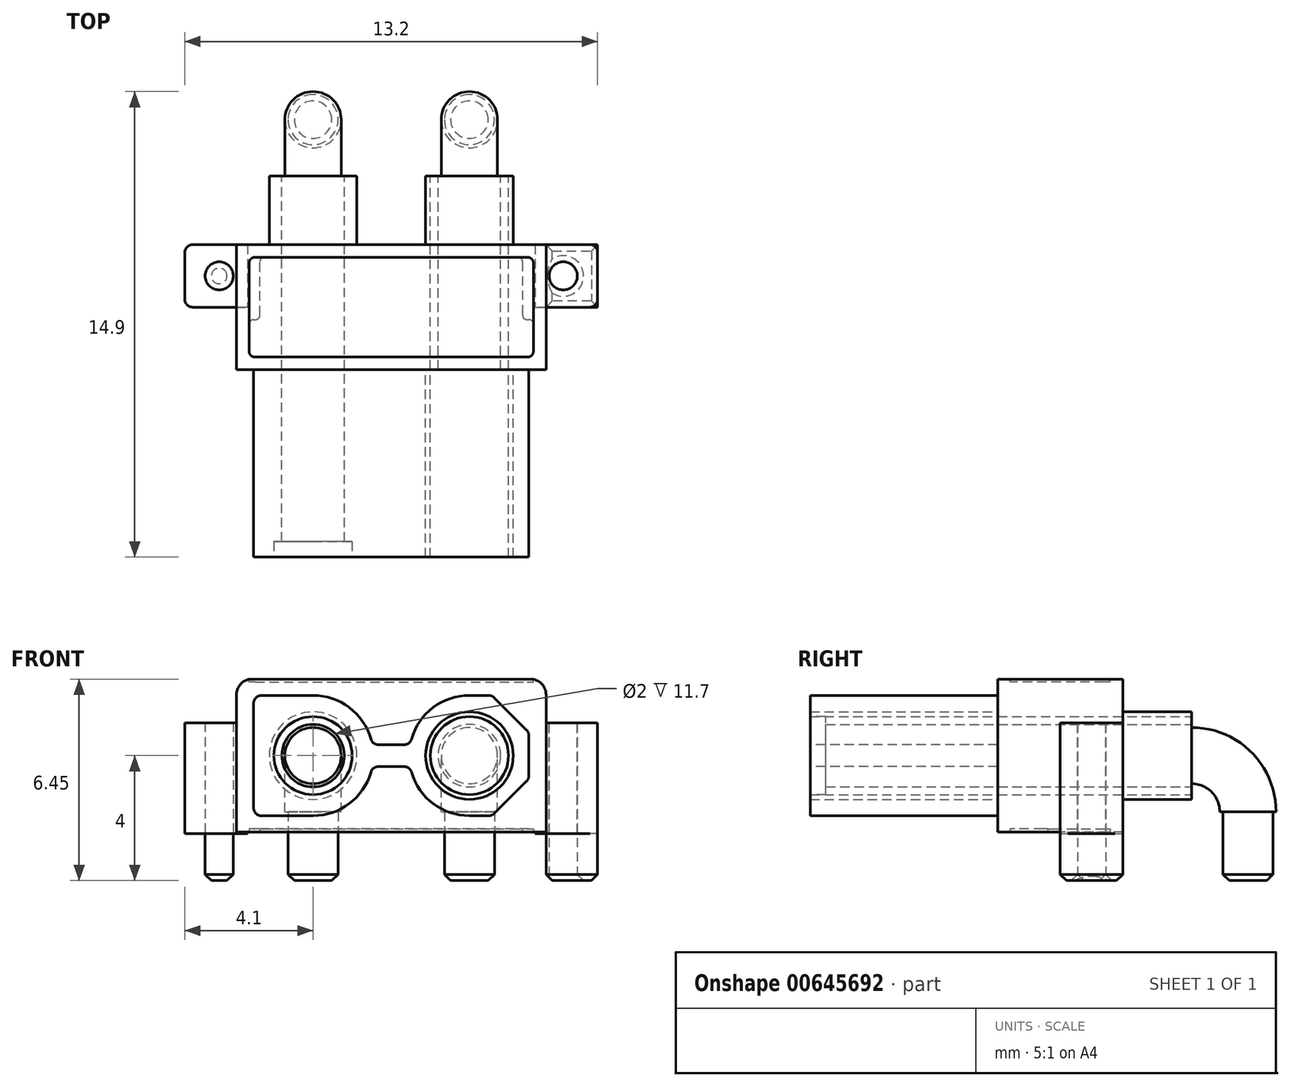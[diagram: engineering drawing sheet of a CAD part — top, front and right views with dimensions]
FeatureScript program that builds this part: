
annotation { "Feature Type Name" : "Feature", "Feature Type Description" : "" }
export const myFeature = defineFeature(function(context is Context, id is Id, definition is map)
    precondition{}
    {
        {
            var Q0;
            Q0=qCreatedBy(makeId("Front.planeOp"),FACE);
            var sketch = newSketch(context, id + "F0", { "sketchPlane" : qUnion([Q0])});
            skLineSegment(sketch, "E0", {"start": v(-2.5, 0) * mm, "end": v(2.5, 0) * mm, "construction": true});
            skCircle(sketch, "E1", {"center": v(2.5, 0) * mm, "radius": 1.25 * mm});
            skCircle(sketch, "E2", {"center": v(-2.5, 0) * mm, "radius": 1.25 * mm});
            skCircle(sketch, "E3", {"center": v(-2.5, 0) * mm, "radius": 1 * mm});
            skCircle(sketch, "E4", {"center": v(2.5, 0) * mm, "radius": 1 * mm});
            skSolve(sketch);
        }
        {
            var Q0;
            Q0=qCreatedBy(makeId("Front.planeOp"),FACE);
            var sketch = newSketch(context, id + "F1", { "sketchPlane" : qUnion([Q0])});
            skCircle(sketch, "E5.MirrorC", {"center": v(2.5, 0) * mm, "radius": 1.25 * mm});
            skCircle(sketch, "E6.MirrorC", {"center": v(-2.5, 0) * mm, "radius": 1.4 * mm});
            skLineSegment(sketch, "E7.MirrorCS", {"start": v(3.23, -1.93) * mm, "end": v(2.5, -1.93) * mm});
            skArc(sketch, "E8.MirrorCS", {"start": v(2.5, -1.93) * mm, "mid": v(1.27, -1.48) * mm, "end": v(0.6, -0.35) * mm});
            skCircle(sketch, "E9.MirrorC", {"center": v(-2.5, 0) * mm, "radius": 1.25 * mm});
            skArc(sketch, "E10.MirrorCS", {"start": v(-0.6, -0.35) * mm, "mid": v(-1.27, -1.48) * mm, "end": v(-2.5, -1.93) * mm});
            skCircle(sketch, "E11.MirrorC", {"center": v(2.5, 0) * mm, "radius": 1.4 * mm});
            skLineSegment(sketch, "E12.MirrorCS", {"start": v(0.6, 0.35) * mm, "end": v(-0.6, 0.35) * mm});
            skLineSegment(sketch, "E13.MirrorCS", {"start": v(-0.6, -0.35) * mm, "end": v(0.6, -0.35) * mm});
            skLineSegment(sketch, "E14.MirrorCS", {"start": v(2.5, 1.93) * mm, "end": v(3.23, 1.93) * mm});
            skLineSegment(sketch, "E15.MirrorCS", {"start": v(3.23, 1.92) * mm, "end": v(4.4, 0.75) * mm});
            skLineSegment(sketch, "E16.MirrorCS", {"start": v(4.4, 0) * mm, "end": v(-4.4, 0) * mm, "construction": true});
            skLineSegment(sketch, "E17.MirrorCS", {"start": v(-2.5, 1.92) * mm, "end": v(-4.4, 1.92) * mm});
            skLineSegment(sketch, "E18.MirrorCS", {"start": v(4.4, 0.75) * mm, "end": v(4.4, -0.75) * mm});
            skLineSegment(sketch, "E19.MirrorCS", {"start": v(4.4, -0.75) * mm, "end": v(3.23, -1.93) * mm});
            skLineSegment(sketch, "E20.MirrorCS", {"start": v(0, -0.35) * mm, "end": v(0, 0.35) * mm, "construction": true});
            skArc(sketch, "E21.MirrorCS", {"start": v(0.6, 0.35) * mm, "mid": v(1.27, 1.48) * mm, "end": v(2.5, 1.93) * mm});
            skLineSegment(sketch, "E22.MirrorCS", {"start": v(-4.4, 1.92) * mm, "end": v(-4.4, -1.93) * mm});
            skLineSegment(sketch, "E23.MirrorCS", {"start": v(-4.4, -1.93) * mm, "end": v(-2.5, -1.93) * mm});
            skArc(sketch, "E24.MirrorCS", {"start": v(-2.5, 1.93) * mm, "mid": v(-1.27, 1.48) * mm, "end": v(-0.6, 0.35) * mm});
            skSolve(sketch);
        }
        {
            var Q0;
            Q0=qCreatedBy(makeId("Front.planeOp"),FACE);
            var sketch = newSketch(context, id + "F2", { "sketchPlane" : qUnion([Q0])});
            skLineSegment(sketch, "E25.bottom", {"start": v(-4.45, 2.45) * mm, "end": v(4.45, 2.45) * mm});
            skLineSegment(sketch, "E25.top", {"start": v(-4.95, -2.45) * mm, "end": v(4.95, -2.45) * mm});
            skLineSegment(sketch, "E25.left", {"start": v(-4.95, 1.95) * mm, "end": v(-4.95, -2.45) * mm});
            skLineSegment(sketch, "E25.right", {"start": v(4.95, 1.95) * mm, "end": v(4.95, -2.45) * mm});
            skPoint(sketch, "E25.middle", {"position": v(0, 0) * mm});
            skPoint(sketch, "E26.visualSharp", {"position": v(4.95, 2.45) * mm});
            skArc(sketch, "E26.filletArc", {"start": v(4.95, 1.95) * mm, "mid": v(4.8, 2.3) * mm, "end": v(4.45, 2.45) * mm});
            skPoint(sketch, "E27.visualSharp", {"position": v(-4.95, 2.45) * mm});
            skArc(sketch, "E27.filletArc", {"start": v(-4.45, 2.45) * mm, "mid": v(-4.8, 2.3) * mm, "end": v(-4.95, 1.95) * mm});
            skCircle(sketch, "E28.0", {"center": v(2.5, 0) * mm, "radius": 1.25 * mm});
            skCircle(sketch, "E28.1", {"center": v(-2.5, 0) * mm, "radius": 1.25 * mm});
            skSolve(sketch);
        }
        {
            var Q0;
            Q0=makeQuery(id+"F0.imprint","IMPRINT",FACE,{"disambiguationData":[TD([[makeQuery(id+"F0.imprint","IMPRINT",EDGE,{"derivedFrom":sQuery(id+"F0.wireOp",EDGE,"E2")}),1.0]])]});
            var Q1;
            Q1=makeQuery(id+"F0.imprint","IMPRINT",FACE,{"disambiguationData":[TD([[makeQuery(id+"F0.imprint","IMPRINT",EDGE,{"derivedFrom":sQuery(id+"F0.wireOp",EDGE,"E1")}),1.0]])]});
            extrude(context, id + "F3", {"entities" : qUnion([Q0, Q1]), "depth" : 5.5 * mm, "offsetDistance" : 25 * mm});
        }
        {
            var Q0;
            Q0=qCreatedBy(makeId("Right.planeOp"),FACE);
            var sketch = newSketch(context, id + "F4", { "sketchPlane" : qUnion([Q0])});
            skLineSegment(sketch, "E29", {"start": v(0, 0) * mm, "end": v(6.2, 0) * mm});
            skArc(sketch, "E30", {"start": v(6.2, 0) * mm, "mid": v(7.47, -0.53) * mm, "end": v(8, -1.8) * mm});
            skLineSegment(sketch, "E31", {"start": v(8, -1.8) * mm, "end": v(8, -4) * mm});
            skLineSegment(sketch, "E32", {"start": v(8.8, -4) * mm, "end": v(7.2, -4) * mm, "construction": true});
            skLineSegment(sketch, "E33", {"start": v(8.9, -1.8) * mm, "end": v(7.1, -1.8) * mm, "construction": true});
            skLineSegment(sketch, "E34", {"start": v(6.2, 1.25) * mm, "end": v(6.2, -1.25) * mm, "construction": true});
            skLineSegment(sketch, "E35", {"start": v(7.2, -4) * mm, "end": v(7.2, -1.8) * mm, "construction": true});
            skLineSegment(sketch, "E36", {"start": v(8.8, -4) * mm, "end": v(8.8, -1.8) * mm, "construction": true});
            skArc(sketch, "E37", {"start": v(7.1, -1.8) * mm, "mid": v(6.84, -1.16) * mm, "end": v(6.2, -0.9) * mm, "construction": true});
            skArc(sketch, "E38", {"start": v(8.9, -1.8) * mm, "mid": v(8.1, 0.1) * mm, "end": v(6.2, 0.9) * mm, "construction": true});
            skLineSegment(sketch, "E39", {"start": v(6.2, 1.25) * mm, "end": v(0, 1.25) * mm, "construction": true});
            skLineSegment(sketch, "E40", {"start": v(6.2, -1.25) * mm, "end": v(0, -1.25) * mm, "construction": true});
            skLineSegment(sketch, "E41.0", {"start": v(0, 1.25) * mm, "end": v(0, -1.25) * mm, "construction": true});
            skLineSegment(sketch, "E42", {"start": v(4, 1.25) * mm, "end": v(4, -1.25) * mm, "construction": true});
            skSolve(sketch);
        }
        {
            var Q0;
            Q0=makeQuery(id+"F1.imprint","IMPRINT",FACE,{"disambiguationData":[TD([[makeQuery(id+"F1.imprint","IMPRINT",EDGE,{"derivedFrom":sQuery(id+"F1.wireOp",EDGE,"E5.MirrorC")}),-1.0]])]});
            var Q1;
            Q1=makeQuery(id+"F0.imprint","IMPRINT",FACE,{"disambiguationData":[TD([[makeQuery(id+"F0.imprint","IMPRINT",EDGE,{"derivedFrom":sQuery(id+"F0.wireOp",EDGE,"E4")}),1.0]])]});
            var Q2;
            Q2=makeQuery(id+"F0.imprint","IMPRINT",FACE,{"disambiguationData":[TD([[makeQuery(id+"F0.imprint","IMPRINT",EDGE,{"derivedFrom":sQuery(id+"F0.wireOp",EDGE,"E2")}),1.0]])]});
            var Q3;
            Q3=makeQuery(id+"F1.imprint","IMPRINT",FACE,{"disambiguationData":[TD([[makeQuery(id+"F1.imprint","IMPRINT",EDGE,{"derivedFrom":sQuery(id+"F1.wireOp",EDGE,"E9.MirrorC")}),-1.0]])]});
            var Q4;
            Q4=sQuery(id+"F4.wireOp",EDGE,"E29");
            sweep(context, id + "F5", {"operationType" : NewBodyOperationType.ADD, "profiles" : qUnion([Q0, Q1, Q2, Q3]), "path" : qUnion([Q4])});
        }
        {
            var Q0;
            {var subQ0=sQuery(id+"F4.wireOp",VERTEX,"E29.end");Q0=makeQuery(id+"F5.boolean.opBoolean","MERGE",FACE,{"derivedFrom":[makeQuery(id+"F5.opSweep","CAP_FACE",FACE,{"disambiguationData":[OSD([sQuery(id+"F0.wireOp",EDGE,"E2"),sQuery(id+"F0.wireOp",EDGE,"E3"),subQ0])],"isStart":false}),makeQuery(id+"F5.opSweep","CAP_FACE",FACE,{"disambiguationData":[OSD([sQuery(id+"F1.wireOp",EDGE,"E9.MirrorC"),subQ0])],"isStart":false})]});}
            var sketch = newSketch(context, id + "F6", { "sketchPlane" : qUnion([Q0])});
            skCircle(sketch, "E43", {"center": v(2.5, 0) * mm, "radius": 0.9 * mm});
            skCircle(sketch, "E44", {"center": v(-2.5, 0) * mm, "radius": 0.9 * mm});
            skLineSegment(sketch, "E45", {"start": v(-2.5, 0.9) * mm, "end": v(2.5, 0.9) * mm, "construction": true});
            skSolve(sketch);
        }
        {
            var Q0;
            Q0=makeQuery(id+"F6.imprint","IMPRINT",FACE,{"disambiguationData":[TD([[makeQuery(id+"F6.imprint","IMPRINT",EDGE,{"derivedFrom":sQuery(id+"F6.wireOp",EDGE,"E44")}),1.0]])]});
            var Q1;
            Q1=makeQuery(id+"F6.imprint","IMPRINT",FACE,{"disambiguationData":[TD([[makeQuery(id+"F6.imprint","IMPRINT",EDGE,{"derivedFrom":sQuery(id+"F6.wireOp",EDGE,"E43")}),1.0]])]});
            var Q2;
            Q2=sQuery(id+"F4.wireOp",EDGE,"E30");
            sweep(context, id + "F7", {"operationType" : NewBodyOperationType.ADD, "profiles" : qUnion([Q0, Q1]), "path" : qUnion([Q2])});
        }
        {
            var Q0;
            Q0=makeQuery(id+"F7.opSweep","CAP_FACE",FACE,{"disambiguationData":[OSD([sQuery(id+"F4.wireOp",VERTEX,"E30.end"),sQuery(id+"F6.wireOp",EDGE,"E43")])],"isStart":false});
            var sketch = newSketch(context, id + "F8", { "sketchPlane" : qUnion([Q0])});
            skCircle(sketch, "E46", {"center": v(-2.5, -8) * mm, "radius": 0.8 * mm});
            skCircle(sketch, "E47", {"center": v(2.5, -8) * mm, "radius": 0.8 * mm});
            skLineSegment(sketch, "E48", {"start": v(2.5, -8.8) * mm, "end": v(-2.5, -8.8) * mm, "construction": true});
            skSolve(sketch);
        }
        {
            var Q0;
            Q0=makeQuery(id+"F8.imprint","IMPRINT",FACE,{"disambiguationData":[TD([[makeQuery(id+"F8.imprint","IMPRINT",EDGE,{"derivedFrom":sQuery(id+"F8.wireOp",EDGE,"E47")}),1.0]])]});
            var Q1;
            Q1=makeQuery(id+"F8.imprint","IMPRINT",FACE,{"disambiguationData":[TD([[makeQuery(id+"F8.imprint","IMPRINT",EDGE,{"derivedFrom":sQuery(id+"F8.wireOp",EDGE,"E46")}),1.0]])]});
            var Q2;
            Q2=sQuery(id+"F4.wireOp",EDGE,"E31");
            sweep(context, id + "F9", {"operationType" : NewBodyOperationType.ADD, "profiles" : qUnion([Q0, Q1]), "path" : qUnion([Q2])});
        }
        {
            var Q0;
            Q0=makeQuery(id+"F2.imprint","IMPRINT",FACE,{"disambiguationData":[TD([[makeQuery(id+"F2.imprint","IMPRINT",EDGE,{"derivedFrom":sQuery(id+"F2.wireOp",EDGE,"E25.bottom")}),-1.0]])]});
            extrude(context, id + "F10", {"entities" : qUnion([Q0]), "oppositeDirection" : true, "depth" : 4 * mm, "offsetDistance" : 25 * mm});
        }
        {
            var Q0;
            Q0=makeQuery(id+"F1.imprint","IMPRINT",FACE,{"disambiguationData":[TD([[makeQuery(id+"F1.imprint","IMPRINT",EDGE,{"derivedFrom":sQuery(id+"F1.wireOp",EDGE,"E6.MirrorC")}),-1.0]])]});
            var Q1;
            Q1=makeQuery(id+"F1.imprint","IMPRINT",FACE,{"disambiguationData":[TD([[makeQuery(id+"F1.imprint","IMPRINT",EDGE,{"derivedFrom":sQuery(id+"F1.wireOp",EDGE,"E6.MirrorC")}),1.0]])]});
            var Q2;
            Q2=makeQuery(id+"F1.imprint","IMPRINT",FACE,{"disambiguationData":[TD([[makeQuery(id+"F1.imprint","IMPRINT",EDGE,{"derivedFrom":sQuery(id+"F1.wireOp",EDGE,"E5.MirrorC")}),1.0]])]});
            extrude(context, id + "F11", {"entities" : qUnion([Q0, Q1, Q2]), "operationType" : NewBodyOperationType.ADD, "depth" : 6 * mm, "offsetDistance" : 25 * mm});
        }
        {
            var Q0;
            Q0=makeQuery(id+"F10.opExtrude","SWEPT_FACE",FACE,{"disambiguationData":[OSD([sQuery(id+"F2.wireOp",EDGE,"E25.top")])]});
            var sketch = newSketch(context, id + "F12", { "sketchPlane" : qUnion([Q0])});
            skLineSegment(sketch, "E49", {"start": v(-4.95, -4) * mm, "end": v(-6.6, -4) * mm});
            skLineSegment(sketch, "E50", {"start": v(-6.6, -4) * mm, "end": v(-6.6, -2) * mm});
            skLineSegment(sketch, "E51", {"start": v(-6.6, -2) * mm, "end": v(-4.95, -2) * mm});
            skCircle(sketch, "E52", {"center": v(-5.5, -3) * mm, "radius": 0.45 * mm});
            skLineSegment(sketch, "E53", {"start": v(-5.5, -4) * mm, "end": v(-5.5, -2) * mm, "construction": true});
            skLineSegment(sketch, "E54.MirrorCS", {"start": v(6.6, -2) * mm, "end": v(4.95, -2) * mm});
            skCircle(sketch, "E55.MirrorC", {"center": v(5.5, -3) * mm, "radius": 0.45 * mm});
            skLineSegment(sketch, "E56.MirrorCS", {"start": v(4.95, -4) * mm, "end": v(6.6, -4) * mm});
            skLineSegment(sketch, "E57.MirrorCS", {"start": v(6.6, -4) * mm, "end": v(6.6, -2) * mm});
            skLineSegment(sketch, "E58", {"start": v(-4.95, -2) * mm, "end": v(-4.6, -2) * mm});
            skLineSegment(sketch, "E59", {"start": v(-4.6, -2) * mm, "end": v(-4.6, -4) * mm});
            skLineSegment(sketch, "E60.MirrorCS", {"start": v(4.95, -2) * mm, "end": v(4.6, -2) * mm});
            skLineSegment(sketch, "E61.MirrorCS", {"start": v(4.6, -2) * mm, "end": v(4.6, -4) * mm});
            skSolve(sketch);
        }
        {
            var Q0;
            {var subQ0=sQuery(id+"F12.wireOp",EDGE,"E58");Q0=makeQuery(id+"F12.imprint","IMPRINT",FACE,{"disambiguationData":[TD([[makeQuery(id+"F12.imprint","IMPRINT",EDGE,{"derivedFrom":subQ0}),-1.0]])]});}
            var Q1;
            {var subQ0=sQuery(id+"F12.wireOp",EDGE,"E49");Q1=makeQuery(id+"F12.imprint","IMPRINT",FACE,{"disambiguationData":[TD([[makeQuery(id+"F12.imprint","IMPRINT",EDGE,{"derivedFrom":subQ0}),-1.0]])]});}
            var Q2;
            {var subQ0=sQuery(id+"F12.wireOp",EDGE,"E60.MirrorCS");Q2=makeQuery(id+"F12.imprint","IMPRINT",FACE,{"disambiguationData":[TD([[makeQuery(id+"F12.imprint","IMPRINT",EDGE,{"derivedFrom":subQ0}),1.0]])]});}
            var Q3;
            {var subQ3=sQuery(id+"F12.wireOp",EDGE,"E54.MirrorCS");Q3=makeQuery(id+"F12.imprint","IMPRINT",FACE,{"disambiguationData":[TD([[makeQuery(id+"F12.imprint","IMPRINT",EDGE,{"derivedFrom":subQ3}),1.0]])]});}
            extrude(context, id + "F13", {"entities" : qUnion([Q0, Q1, Q2, Q3]), "operationType" : NewBodyOperationType.ADD, "depth" : 0.05 * mm, "offsetDistance" : 25 * mm, "hasSecondDirection" : true, "secondDirectionOppositeDirection" : true, "secondDirectionDepth" : 3.5 * mm});
        }
        {
            var Q0;
            Q0=makeQuery(id+"F10.opExtrude","SWEPT_FACE",FACE,{"disambiguationData":[OSD([sQuery(id+"F2.wireOp",EDGE,"E25.top")])]});
            var sketch = newSketch(context, id + "F14", { "sketchPlane" : qUnion([Q0])});
            skLineSegment(sketch, "E62.0", {"start": v(-4.05, -3.6) * mm, "end": v(4.05, -3.6) * mm});
            skLineSegment(sketch, "E62.1", {"start": v(-4.2, -1.75) * mm, "end": v(-4.2, -3.45) * mm});
            skLineSegment(sketch, "E62.2", {"start": v(4.2, -3.45) * mm, "end": v(4.2, -1.75) * mm});
            skLineSegment(sketch, "E62.3", {"start": v(-4.4, -1.6) * mm, "end": v(-4.35, -1.6) * mm});
            skLineSegment(sketch, "E62.4", {"start": v(4.35, -1.6) * mm, "end": v(4.4, -1.6) * mm});
            skLineSegment(sketch, "E62.5", {"start": v(4.55, -1.45) * mm, "end": v(4.55, -0.55) * mm});
            skLineSegment(sketch, "E62.6", {"start": v(4.4, -0.4) * mm, "end": v(-4.4, -0.4) * mm});
            skLineSegment(sketch, "E62.7", {"start": v(-4.55, -0.55) * mm, "end": v(-4.55, -1.45) * mm});
            skPoint(sketch, "E63.visualSharp", {"position": v(-4.2, -1.6) * mm});
            skArc(sketch, "E63.filletArc", {"start": v(-4.2, -1.75) * mm, "mid": v(-4.24, -1.64) * mm, "end": v(-4.35, -1.6) * mm});
            skPoint(sketch, "E64.visualSharp", {"position": v(-4.55, -0.4) * mm});
            skArc(sketch, "E64.filletArc", {"start": v(-4.4, -0.4) * mm, "mid": v(-4.5, -0.44) * mm, "end": v(-4.55, -0.55) * mm});
            skPoint(sketch, "E65.visualSharp", {"position": v(-4.55, -1.6) * mm});
            skArc(sketch, "E65.filletArc", {"start": v(-4.55, -1.45) * mm, "mid": v(-4.5, -1.56) * mm, "end": v(-4.4, -1.6) * mm});
            skPoint(sketch, "E66.visualSharp", {"position": v(-4.2, -3.6) * mm});
            skArc(sketch, "E66.filletArc", {"start": v(-4.2, -3.45) * mm, "mid": v(-4.16, -3.56) * mm, "end": v(-4.05, -3.6) * mm});
            skPoint(sketch, "E67.visualSharp", {"position": v(4.2, -3.6) * mm});
            skArc(sketch, "E67.filletArc", {"start": v(4.05, -3.6) * mm, "mid": v(4.16, -3.56) * mm, "end": v(4.2, -3.45) * mm});
            skPoint(sketch, "E68.visualSharp", {"position": v(4.2, -1.6) * mm});
            skArc(sketch, "E68.filletArc", {"start": v(4.35, -1.6) * mm, "mid": v(4.24, -1.64) * mm, "end": v(4.2, -1.75) * mm});
            skPoint(sketch, "E69.visualSharp", {"position": v(4.55, -1.6) * mm});
            skArc(sketch, "E69.filletArc", {"start": v(4.4, -1.6) * mm, "mid": v(4.5, -1.56) * mm, "end": v(4.55, -1.45) * mm});
            skPoint(sketch, "E70.visualSharp", {"position": v(4.55, -0.4) * mm});
            skArc(sketch, "E70.filletArc", {"start": v(4.55, -0.55) * mm, "mid": v(4.5, -0.44) * mm, "end": v(4.4, -0.4) * mm});
            skSolve(sketch);
        }
        {
            var Q0;
            Q0=makeQuery(id+"F14.imprint","IMPRINT",FACE,{"disambiguationData":[TD([[makeQuery(id+"F14.imprint","IMPRINT",EDGE,{"derivedFrom":sQuery(id+"F14.wireOp",EDGE,"E62.0")}),1.0]])]});
            extrude(context, id + "F15", {"entities" : qUnion([Q0]), "operationType" : NewBodyOperationType.REMOVE, "oppositeDirection" : true, "depth" : 0.1 * mm, "offsetDistance" : 25 * mm});
        }
        {
            var Q0;
            Q0=makeQuery(id+"F12.imprint","IMPRINT",FACE,{"disambiguationData":[TD([[makeQuery(id+"F12.imprint","IMPRINT",EDGE,{"derivedFrom":sQuery(id+"F12.wireOp",EDGE,"E55.MirrorC")}),-1.0]])]});
            var Q1;
            Q1=makeQuery(id+"F12.imprint","IMPRINT",FACE,{"disambiguationData":[TD([[makeQuery(id+"F12.imprint","IMPRINT",EDGE,{"derivedFrom":sQuery(id+"F12.wireOp",EDGE,"E52")}),1.0]])]});
            var Q2;
            Q2=makeQuery(id+"F13.opExtrude","CAP_FACE",FACE,{"disambiguationData":[OSD([sQuery(id+"F2.wireOp",EDGE,"E25.top"),sQuery(id+"F12.wireOp",EDGE,"E54.MirrorCS"),sQuery(id+"F12.wireOp",EDGE,"E55.MirrorC"),sQuery(id+"F12.wireOp",EDGE,"E56.MirrorCS"),sQuery(id+"F12.wireOp",EDGE,"E57.MirrorCS"),sQuery(id+"F12.wireOp",EDGE,"E60.MirrorCS"),sQuery(id+"F12.wireOp",EDGE,"E61.MirrorCS")])],"isStart":true});
            var Q3;
            Q3=makeQuery(id+"F9.opSweep","CAP_FACE",FACE,{"disambiguationData":[OSD([sQuery(id+"F4.wireOp",VERTEX,"E31.end"),sQuery(id+"F8.wireOp",EDGE,"E47")])],"isStart":false});
            extrude(context, id + "F16", {"entities" : qUnion([Q0, Q1]), "endBound" : BoundingType.UP_TO_SURFACE, "oppositeDirection" : true, "depth" : 25 * mm, "endBoundEntityFace" : qUnion([Q2]), "offsetDistance" : 25 * mm, "hasSecondDirection" : true, "secondDirectionBound" : BoundingType.UP_TO_SURFACE, "secondDirectionOppositeDirection" : false, "secondDirectionDepth" : 25 * mm, "secondDirectionBoundEntityFace" : qUnion([Q3])});
        }
        {
            var Q0;
            Q0=makeQuery(id+"F10.opExtrude","SWEPT_FACE",FACE,{"disambiguationData":[OSD([sQuery(id+"F2.wireOp",EDGE,"E25.bottom")])]});
            var sketch = newSketch(context, id + "F17", { "sketchPlane" : qUnion([Q0])});
            skLineSegment(sketch, "E71.bottom", {"start": v(-4.95, 4) * mm, "end": v(4.95, 4) * mm, "construction": true});
            skLineSegment(sketch, "E71.top", {"start": v(-4.95, 0) * mm, "end": v(4.95, 0) * mm, "construction": true});
            skLineSegment(sketch, "E71.left", {"start": v(-4.95, 4) * mm, "end": v(-4.95, 0) * mm, "construction": true});
            skLineSegment(sketch, "E71.right", {"start": v(4.95, 4) * mm, "end": v(4.95, 0) * mm, "construction": true});
            skPoint(sketch, "E71.middle", {"position": v(0, 2) * mm});
            skLineSegment(sketch, "E72.0", {"start": v(-4.35, 0.4) * mm, "end": v(4.35, 0.4) * mm});
            skLineSegment(sketch, "E72.1", {"start": v(-4.55, 3.4) * mm, "end": v(-4.55, 0.6) * mm});
            skLineSegment(sketch, "E72.2", {"start": v(-4.35, 3.6) * mm, "end": v(4.35, 3.6) * mm});
            skLineSegment(sketch, "E72.3", {"start": v(4.55, 3.4) * mm, "end": v(4.55, 0.6) * mm});
            skPoint(sketch, "E73.visualSharp", {"position": v(-4.55, 3.6) * mm});
            skArc(sketch, "E73.filletArc", {"start": v(-4.35, 3.6) * mm, "mid": v(-4.5, 3.54) * mm, "end": v(-4.55, 3.4) * mm});
            skPoint(sketch, "E74.visualSharp", {"position": v(-4.55, 0.4) * mm});
            skArc(sketch, "E74.filletArc", {"start": v(-4.55, 0.6) * mm, "mid": v(-4.5, 0.46) * mm, "end": v(-4.35, 0.4) * mm});
            skPoint(sketch, "E75.visualSharp", {"position": v(4.55, 0.4) * mm});
            skArc(sketch, "E75.filletArc", {"start": v(4.35, 0.4) * mm, "mid": v(4.5, 0.46) * mm, "end": v(4.55, 0.6) * mm});
            skPoint(sketch, "E76.visualSharp", {"position": v(4.55, 3.6) * mm});
            skArc(sketch, "E76.filletArc", {"start": v(4.55, 3.4) * mm, "mid": v(4.5, 3.54) * mm, "end": v(4.35, 3.6) * mm});
            skSolve(sketch);
        }
        {
            var Q0;
            {var subQ6=sQuery(id+"F17.wireOp",EDGE,"E72.0");Q0=makeQuery(id+"F17.imprint","IMPRINT",FACE,{"disambiguationData":[TD([[makeQuery(id+"F17.imprint","IMPRINT",EDGE,{"derivedFrom":subQ6}),1.0]])]});}
            var Q1;
            {var subQ0=sQuery(id+"F17.wireOp",EDGE,"E72.1");Q1=makeQuery(id+"F17.imprint","IMPRINT",FACE,{"disambiguationData":[TD([[makeQuery(id+"F17.imprint","IMPRINT",EDGE,{"derivedFrom":subQ0}),1.0]])]});}
            var Q2;
            {var subQ0=sQuery(id+"F17.wireOp",EDGE,"E72.3");Q2=makeQuery(id+"F17.imprint","IMPRINT",FACE,{"disambiguationData":[TD([[makeQuery(id+"F17.imprint","IMPRINT",EDGE,{"derivedFrom":subQ0}),-1.0]])]});}
            extrude(context, id + "F18", {"entities" : qUnion([Q0, Q1, Q2]), "operationType" : NewBodyOperationType.REMOVE, "oppositeDirection" : true, "depth" : 0.1 * mm, "offsetDistance" : 25 * mm});
        }
        {
            var Q0;
            Q0=makeQuery(id+"F11.opExtrude","SWEPT_EDGE",EDGE,{"disambiguationData":[OSD([sQuery(id+"F1.wireOp",EDGE,"E17.MirrorCS"),sQuery(id+"F1.wireOp",EDGE,"E22.MirrorCS")])]});
            var Q1;
            Q1=makeQuery(id+"F11.opExtrude","SWEPT_EDGE",EDGE,{"disambiguationData":[OSD([sQuery(id+"F1.wireOp",EDGE,"E22.MirrorCS"),sQuery(id+"F1.wireOp",EDGE,"E23.MirrorCS")])]});
            var Q2;
            Q2=makeQuery(id+"F11.opExtrude","SWEPT_EDGE",EDGE,{"disambiguationData":[OSD([sQuery(id+"F1.wireOp",EDGE,"E14.MirrorCS"),sQuery(id+"F1.wireOp",EDGE,"E15.MirrorCS")])]});
            var Q3;
            Q3=makeQuery(id+"F11.opExtrude","SWEPT_EDGE",EDGE,{"disambiguationData":[OSD([sQuery(id+"F1.wireOp",EDGE,"E15.MirrorCS"),sQuery(id+"F1.wireOp",EDGE,"E18.MirrorCS")])]});
            var Q4;
            Q4=makeQuery(id+"F11.opExtrude","SWEPT_EDGE",EDGE,{"disambiguationData":[OSD([sQuery(id+"F1.wireOp",EDGE,"E18.MirrorCS"),sQuery(id+"F1.wireOp",EDGE,"E19.MirrorCS")])]});
            var Q5;
            Q5=makeQuery(id+"F11.opExtrude","SWEPT_EDGE",EDGE,{"disambiguationData":[OSD([sQuery(id+"F1.wireOp",EDGE,"E7.MirrorCS"),sQuery(id+"F1.wireOp",EDGE,"E19.MirrorCS")])]});
            var Q6;
            Q6=makeQuery(id+"F11.opExtrude","SWEPT_EDGE",EDGE,{"disambiguationData":[OSD([sQuery(id+"F1.wireOp",EDGE,"E8.MirrorCS"),sQuery(id+"F1.wireOp",EDGE,"E13.MirrorCS")])]});
            var Q7;
            Q7=makeQuery(id+"F11.opExtrude","SWEPT_EDGE",EDGE,{"disambiguationData":[OSD([sQuery(id+"F1.wireOp",EDGE,"E10.MirrorCS"),sQuery(id+"F1.wireOp",EDGE,"E13.MirrorCS")])]});
            var Q8;
            Q8=makeQuery(id+"F11.opExtrude","SWEPT_EDGE",EDGE,{"disambiguationData":[OSD([sQuery(id+"F1.wireOp",EDGE,"E12.MirrorCS"),sQuery(id+"F1.wireOp",EDGE,"E24.MirrorCS")])]});
            var Q9;
            Q9=makeQuery(id+"F11.opExtrude","SWEPT_EDGE",EDGE,{"disambiguationData":[OSD([sQuery(id+"F1.wireOp",EDGE,"E12.MirrorCS"),sQuery(id+"F1.wireOp",EDGE,"E21.MirrorCS")])]});
            var Q10;
            Q10=makeQuery(id+"F13.opExtrude","SWEPT_EDGE",EDGE,{"disambiguationData":[OSD([sQuery(id+"F12.wireOp",EDGE,"E56.MirrorCS"),sQuery(id+"F12.wireOp",EDGE,"E57.MirrorCS")])]});
            var Q11;
            Q11=makeQuery(id+"F13.opExtrude","SWEPT_EDGE",EDGE,{"disambiguationData":[OSD([sQuery(id+"F12.wireOp",EDGE,"E54.MirrorCS"),sQuery(id+"F12.wireOp",EDGE,"E57.MirrorCS")])]});
            var Q12;
            Q12=makeQuery(id+"F13.opExtrude","SWEPT_EDGE",EDGE,{"disambiguationData":[OSD([sQuery(id+"F12.wireOp",EDGE,"E50"),sQuery(id+"F12.wireOp",EDGE,"E51")])]});
            var Q13;
            Q13=makeQuery(id+"F13.opExtrude","SWEPT_EDGE",EDGE,{"disambiguationData":[OSD([sQuery(id+"F12.wireOp",EDGE,"E49"),sQuery(id+"F12.wireOp",EDGE,"E50")])]});
            fillet(context, id + "F19", {"entities" : qUnion([Q0, Q1, Q2, Q3, Q4, Q5, Q6, Q7, Q8, Q9, Q10, Q11, Q12, Q13]), "radius" : 0.25 * mm, "tangentPropagation" : true, "defaultsChanged" : false, "vertexSettings" : [], "allowEdgeOverflow" : false});
        }
        {
            var Q0;
            Q0=makeQuery(id+"F9.opSweep","CAP_FACE",FACE,{"disambiguationData":[OSD([sQuery(id+"F4.wireOp",VERTEX,"E31.end"),sQuery(id+"F8.wireOp",EDGE,"E46")])],"isStart":false});
            var Q1;
            Q1=makeQuery(id+"F16.opExtrude","CAP_FACE",FACE,{"disambiguationData":[OSD([sQuery(id+"F12.wireOp",EDGE,"E52")])],"isStart":true});
            var Q2;
            Q2=makeQuery(id+"F9.opSweep","CAP_FACE",FACE,{"disambiguationData":[OSD([sQuery(id+"F4.wireOp",VERTEX,"E31.end"),sQuery(id+"F8.wireOp",EDGE,"E47")])],"isStart":false});
            var Q3;
            Q3=makeQuery(id+"F16.opExtrude","CAP_FACE",FACE,{"disambiguationData":[OSD([sQuery(id+"F12.wireOp",EDGE,"E55.MirrorC")])],"isStart":true});
            chamfer(context, id + "F20", {"entities" : qUnion([Q0, Q1, Q2, Q3]), "width" : 0.2 * mm, "tangentPropagation" : true});
        }
    });
